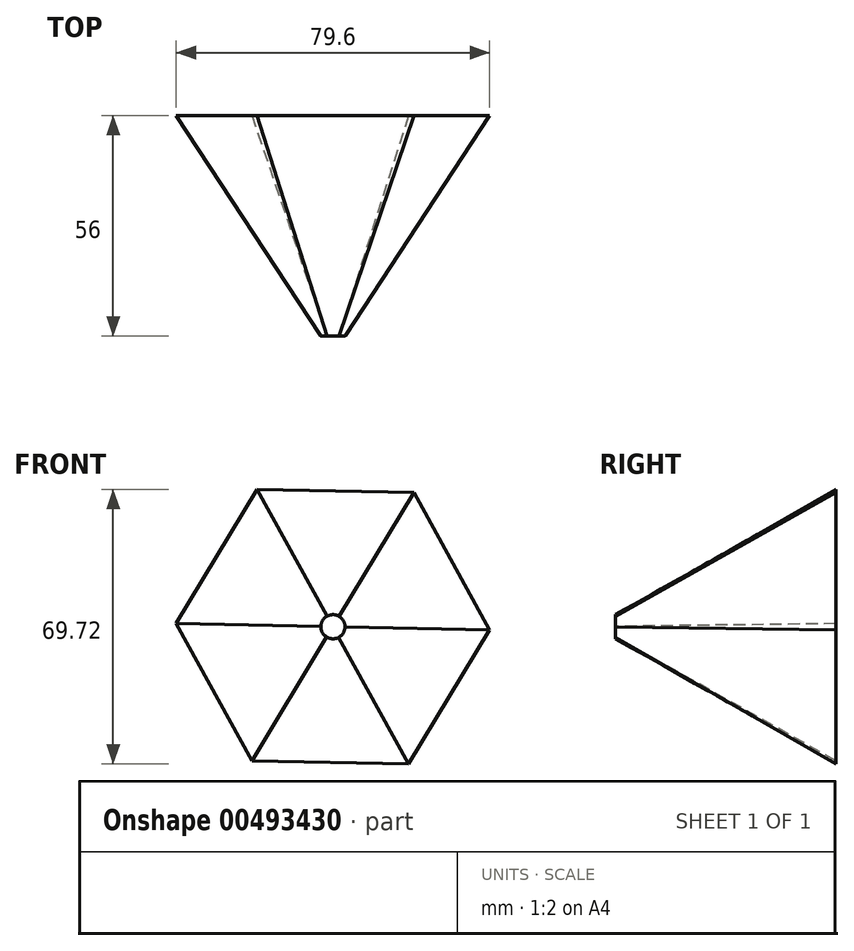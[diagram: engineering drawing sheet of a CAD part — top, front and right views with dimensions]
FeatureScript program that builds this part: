
annotation { "Feature Type Name" : "Feature", "Feature Type Description" : "" }
export const myFeature = defineFeature(function(context is Context, id is Id, definition is map)
    precondition{}
    {
        {
            var Q0;
            Q0=qCreatedBy(makeId("Front.planeOp"),FACE);
            var sketch = newSketch(context, id + "F0", { "sketchPlane" : qUnion([Q0])});
            skCircle(sketch, "E0.cCircle", {"center": v(0, 0) * mm, "radius": 39.8 * mm, "construction": true});
            skLineSegment(sketch, "E0.0", {"start": v(-19.22, 34.86) * mm, "end": v(20.58, 34.07) * mm});
            skLineSegment(sketch, "E0.1", {"start": v(20.58, 34.07) * mm, "end": v(39.8, -0.78) * mm});
            skLineSegment(sketch, "E0.2", {"start": v(39.8, -0.78) * mm, "end": v(19.22, -34.86) * mm});
            skLineSegment(sketch, "E0.3", {"start": v(19.22, -34.86) * mm, "end": v(-20.58, -34.07) * mm});
            skLineSegment(sketch, "E0.4", {"start": v(-20.58, -34.07) * mm, "end": v(-39.8, 0.78) * mm});
            skLineSegment(sketch, "E0.5", {"start": v(-39.8, 0.78) * mm, "end": v(-19.22, 34.86) * mm});
            skSolve(sketch);
        }
        {
            var Q0;
            Q0=qCreatedBy(makeId("Front.planeOp"),FACE);
            cPlane(context, id + "F1", {"entities" : qUnion([Q0]), "cplaneType" : CPlaneType.OFFSET, "offset" : 56 * mm, "width" : 150 * mm, "height" : 150 * mm});
        }
        {
            var Q0;
            Q0=qCreatedBy(id+"F1.planeOp",FACE);
            var sketch = newSketch(context, id + "F2", { "sketchPlane" : qUnion([Q0])});
            skCircle(sketch, "E1", {"center": v(0, 0) * mm, "radius": 3.07 * mm});
            skSolve(sketch);
        }
        {
            var Q0;
            Q0=makeQuery(id+"F0.imprint","IMPRINT",FACE,{"disambiguationData":[TD([[makeQuery(id+"F0.imprint","IMPRINT",EDGE,{"derivedFrom":sQuery(id+"F0.wireOp",EDGE,"E0.0")}),-1.0]])]});
            var Q1;
            Q1=makeQuery(id+"F2.imprint","IMPRINT",FACE,{"disambiguationData":[TD([[makeQuery(id+"F2.imprint","IMPRINT",EDGE,{"derivedFrom":sQuery(id+"F2.wireOp",EDGE,"E1")}),1.0]])]});
            loft(context, id + "F3", {"sheetProfilesArray" : [{ "sheetProfileEntities" : qUnion([Q0]) }, { "sheetProfileEntities" : qUnion([Q1]) }]});
        }
    });
